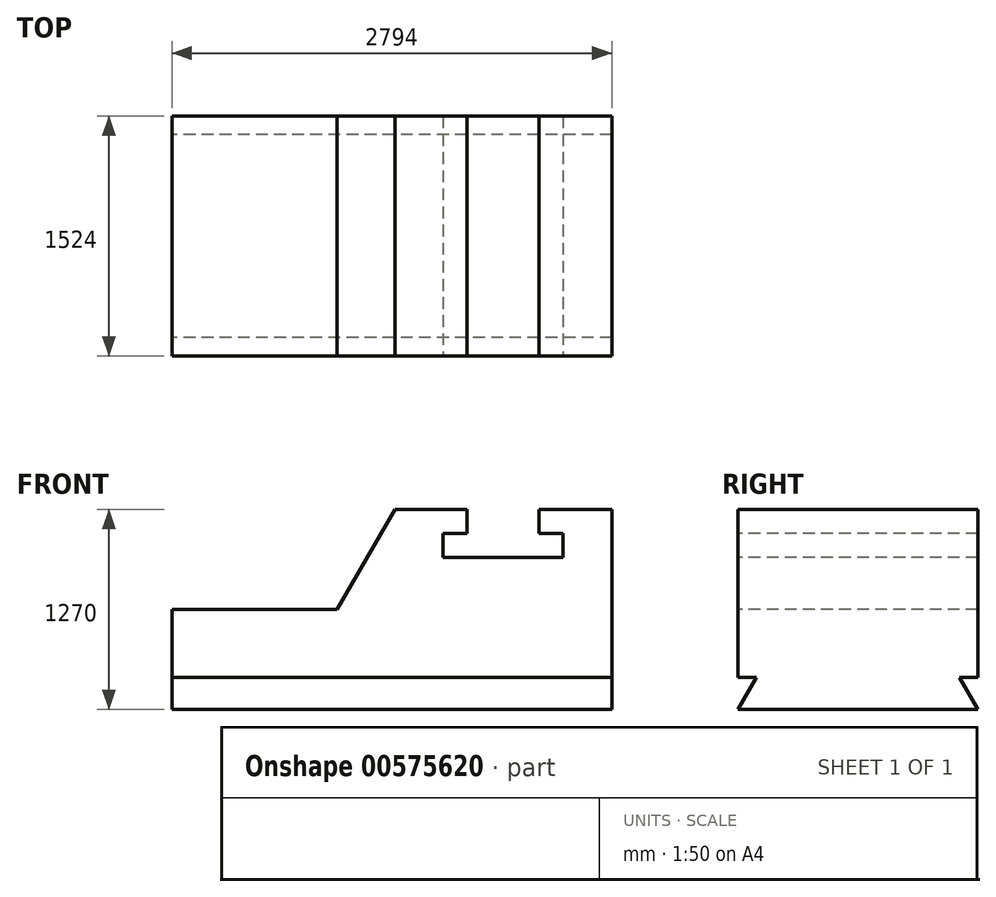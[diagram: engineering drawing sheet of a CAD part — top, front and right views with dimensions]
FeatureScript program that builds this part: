
annotation { "Feature Type Name" : "Feature", "Feature Type Description" : "" }
export const myFeature = defineFeature(function(context is Context, id is Id, definition is map)
    precondition{}
    {
        {
            var Q0;
            Q0=qCreatedBy(makeId("Front.planeOp"),FACE);
            var sketch = newSketch(context, id + "F0", { "sketchPlane" : qUnion([Q0])});
            skLineSegment(sketch, "E0.bottom", {"start": v(0, 0) * mm, "end": v(2794, 0) * mm});
            skLineSegment(sketch, "E0.top", {"start": v(0, 1270) * mm, "end": v(2794, 1270) * mm});
            skLineSegment(sketch, "E0.left", {"start": v(0, 0) * mm, "end": v(0, 1270) * mm});
            skLineSegment(sketch, "E0.right", {"start": v(2794, 0) * mm, "end": v(2794, 1270) * mm});
            skSolve(sketch);
        }
        {
            var Q0;
            Q0=makeQuery(id+"F0.imprint","IMPRINT",FACE,{"disambiguationData":[TD([[makeQuery(id+"F0.imprint","IMPRINT",EDGE,{"derivedFrom":sQuery(id+"F0.wireOp",EDGE,"E0.bottom")}),1.0]])]});
            extrude(context, id + "F1", {"entities" : qUnion([Q0]), "depth" : 1524 * mm, "offsetDistance" : 25.4 * mm});
        }
        {
            var Q0;
            Q0=makeQuery(id+"F1.opExtrude","CAP_FACE",FACE,{"disambiguationData":[OSD([sQuery(id+"F0.wireOp",EDGE,"E0.bottom"),sQuery(id+"F0.wireOp",EDGE,"E0.top"),sQuery(id+"F0.wireOp",EDGE,"E0.left"),sQuery(id+"F0.wireOp",EDGE,"E0.right")])],"isStart":false});
            var sketch = newSketch(context, id + "F2", { "sketchPlane" : qUnion([Q0])});
            skLineSegment(sketch, "E1", {"start": v(1874.15, 1270) * mm, "end": v(1874.15, 1117.6) * mm});
            skLineSegment(sketch, "E2", {"start": v(1874.15, 1117.6) * mm, "end": v(1721.75, 1117.6) * mm});
            skLineSegment(sketch, "E3", {"start": v(1721.75, 1117.6) * mm, "end": v(1721.75, 965.2) * mm});
            skLineSegment(sketch, "E4", {"start": v(1721.75, 965.2) * mm, "end": v(2483.75, 965.2) * mm});
            skLineSegment(sketch, "E5", {"start": v(2483.75, 965.2) * mm, "end": v(2483.75, 1117.6) * mm});
            skLineSegment(sketch, "E6", {"start": v(2483.75, 1117.6) * mm, "end": v(2331.35, 1117.6) * mm});
            skLineSegment(sketch, "E7", {"start": v(2331.35, 1117.6) * mm, "end": v(2331.35, 1270) * mm});
            skLineSegment(sketch, "E8", {"start": v(2331.35, 1270) * mm, "end": v(1874.15, 1270) * mm});
            skSolve(sketch);
        }
        {
            var Q0;
            Q0=makeQuery(id+"F2.imprint","IMPRINT",FACE,{"disambiguationData":[TD([[makeQuery(id+"F2.imprint","IMPRINT",EDGE,{"derivedFrom":sQuery(id+"F2.wireOp",EDGE,"E1")}),1.0]])]});
            extrude(context, id + "F3", {"entities" : qUnion([Q0]), "operationType" : NewBodyOperationType.REMOVE, "endBound" : BoundingType.THROUGH_ALL, "oppositeDirection" : true, "depth" : 25.4 * mm, "offsetDistance" : 25.4 * mm});
        }
        {
            var Q0;
            Q0=makeQuery(id+"F1.opExtrude","CAP_FACE",FACE,{"disambiguationData":[OSD([sQuery(id+"F0.wireOp",EDGE,"E0.bottom"),sQuery(id+"F0.wireOp",EDGE,"E0.top"),sQuery(id+"F0.wireOp",EDGE,"E0.left"),sQuery(id+"F0.wireOp",EDGE,"E0.right")])],"isStart":false});
            var sketch = newSketch(context, id + "F4", { "sketchPlane" : qUnion([Q0])});
            skLineSegment(sketch, "E9", {"start": v(1874.15, 1270) * mm, "end": v(1416.95, 1270) * mm});
            skLineSegment(sketch, "E10", {"start": v(1416.95, 1270) * mm, "end": v(1050.33, 635) * mm});
            skPoint(sketch, "E10.endSnap0", {"position": v(0, 635) * mm});
            skLineSegment(sketch, "E11", {"start": v(0, 635) * mm, "end": v(1551.03, 635) * mm});
            skPoint(sketch, "E11.endSnap0", {"position": v(2794, 635) * mm});
            skSolve(sketch);
        }
        {
            var Q0;
            {var subQ0=sQuery(id+"F4.wireOp",EDGE,"E10");Q0=makeQuery(id+"F4.imprint","IMPRINT",FACE,{"disambiguationData":[TD([[makeQuery(id+"F4.imprint","IMPRINT",EDGE,{"derivedFrom":subQ0}),-1.0]])]});}
            extrude(context, id + "F5", {"entities" : qUnion([Q0]), "operationType" : NewBodyOperationType.REMOVE, "endBound" : BoundingType.THROUGH_ALL, "oppositeDirection" : true, "depth" : 25.4 * mm, "offsetDistance" : 25.4 * mm});
        }
        {
            var Q0;
            Q0=makeQuery(id+"F1.opExtrude","SWEPT_FACE",FACE,{"disambiguationData":[OSD([sQuery(id+"F0.wireOp",EDGE,"E0.left")])]});
            var sketch = newSketch(context, id + "F6", { "sketchPlane" : qUnion([Q0])});
            skLineSegment(sketch, "E12", {"start": v(0, 0) * mm, "end": v(0, 202.1) * mm});
            skLineSegment(sketch, "E13", {"start": v(0, 202.1) * mm, "end": v(116.69, 202.1) * mm});
            skLineSegment(sketch, "E14", {"start": v(116.69, 202.1) * mm, "end": v(0, 0) * mm});
            skSolve(sketch);
        }
        {
            var Q0;
            Q0=makeQuery(id+"F6.imprint","IMPRINT",FACE,{"disambiguationData":[TD([[makeQuery(id+"F6.imprint","IMPRINT",EDGE,{"derivedFrom":sQuery(id+"F6.wireOp",EDGE,"E12")}),-1.0]])]});
            extrude(context, id + "F7", {"entities" : qUnion([Q0]), "operationType" : NewBodyOperationType.REMOVE, "endBound" : BoundingType.THROUGH_ALL, "oppositeDirection" : true, "depth" : 25.4 * mm, "offsetDistance" : 25.4 * mm});
        }
        {
            var Q0;
            Q0=makeQuery(id+"F1.opExtrude","SWEPT_FACE",FACE,{"disambiguationData":[OSD([sQuery(id+"F0.wireOp",EDGE,"E0.left")])]});
            var sketch = newSketch(context, id + "F8", { "sketchPlane" : qUnion([Q0])});
            skLineSegment(sketch, "E15", {"start": v(1524, 0) * mm, "end": v(1524, 203.2) * mm});
            skLineSegment(sketch, "E16", {"start": v(1524, 203.2) * mm, "end": v(1406.68, 203.2) * mm});
            skLineSegment(sketch, "E17", {"start": v(1406.68, 203.2) * mm, "end": v(1524, 0) * mm});
            skSolve(sketch);
        }
        {
            var Q0;
            Q0=makeQuery(id+"F8.imprint","IMPRINT",FACE,{"disambiguationData":[TD([[makeQuery(id+"F8.imprint","IMPRINT",EDGE,{"derivedFrom":sQuery(id+"F8.wireOp",EDGE,"E15")}),1.0]])]});
            extrude(context, id + "F9", {"entities" : qUnion([Q0]), "operationType" : NewBodyOperationType.REMOVE, "endBound" : BoundingType.THROUGH_ALL, "oppositeDirection" : true, "depth" : 25.4 * mm, "offsetDistance" : 25.4 * mm});
        }
    });
